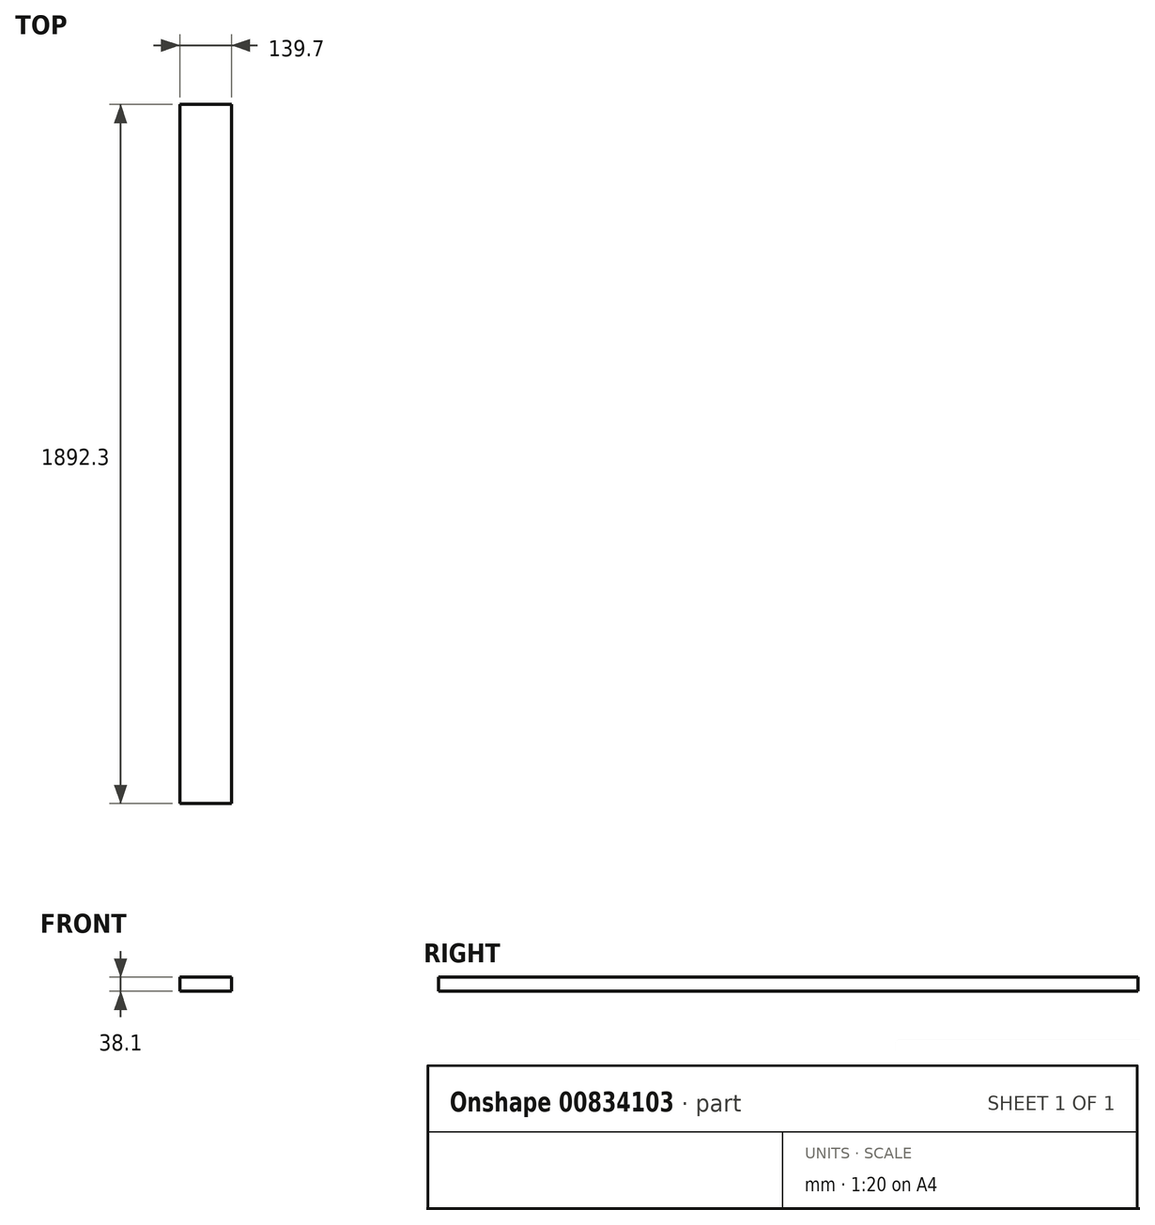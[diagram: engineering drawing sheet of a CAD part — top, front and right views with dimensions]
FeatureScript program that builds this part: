
annotation { "Feature Type Name" : "Feature", "Feature Type Description" : "" }
export const myFeature = defineFeature(function(context is Context, id is Id, definition is map)
    precondition{}
    {
        {
            var Q0;
            Q0=qCreatedBy(makeId("Front.planeOp"),FACE);
            var sketch = newSketch(context, id + "F0", { "sketchPlane" : qUnion([Q0])});
            skLineSegment(sketch, "E0.bottom", {"start": v(69.85, -19.05) * mm, "end": v(-69.85, -19.05) * mm});
            skLineSegment(sketch, "E0.top", {"start": v(69.85, 19.05) * mm, "end": v(-69.85, 19.05) * mm});
            skLineSegment(sketch, "E0.left", {"start": v(69.85, -19.05) * mm, "end": v(69.85, 19.05) * mm});
            skLineSegment(sketch, "E0.right", {"start": v(-69.85, -19.05) * mm, "end": v(-69.85, 19.05) * mm});
            skPoint(sketch, "E0.middle", {"position": v(0, 0) * mm});
            skSolve(sketch);
        }
        {
            var Q0;
            Q0=qSketchRegion(id+"F0",true);
            extrude(context, id + "F1", {"entities" : qUnion([Q0]), "endBound" : BoundingType.SYMMETRIC, "depth" : 1892.3 * mm});
        }
    });
